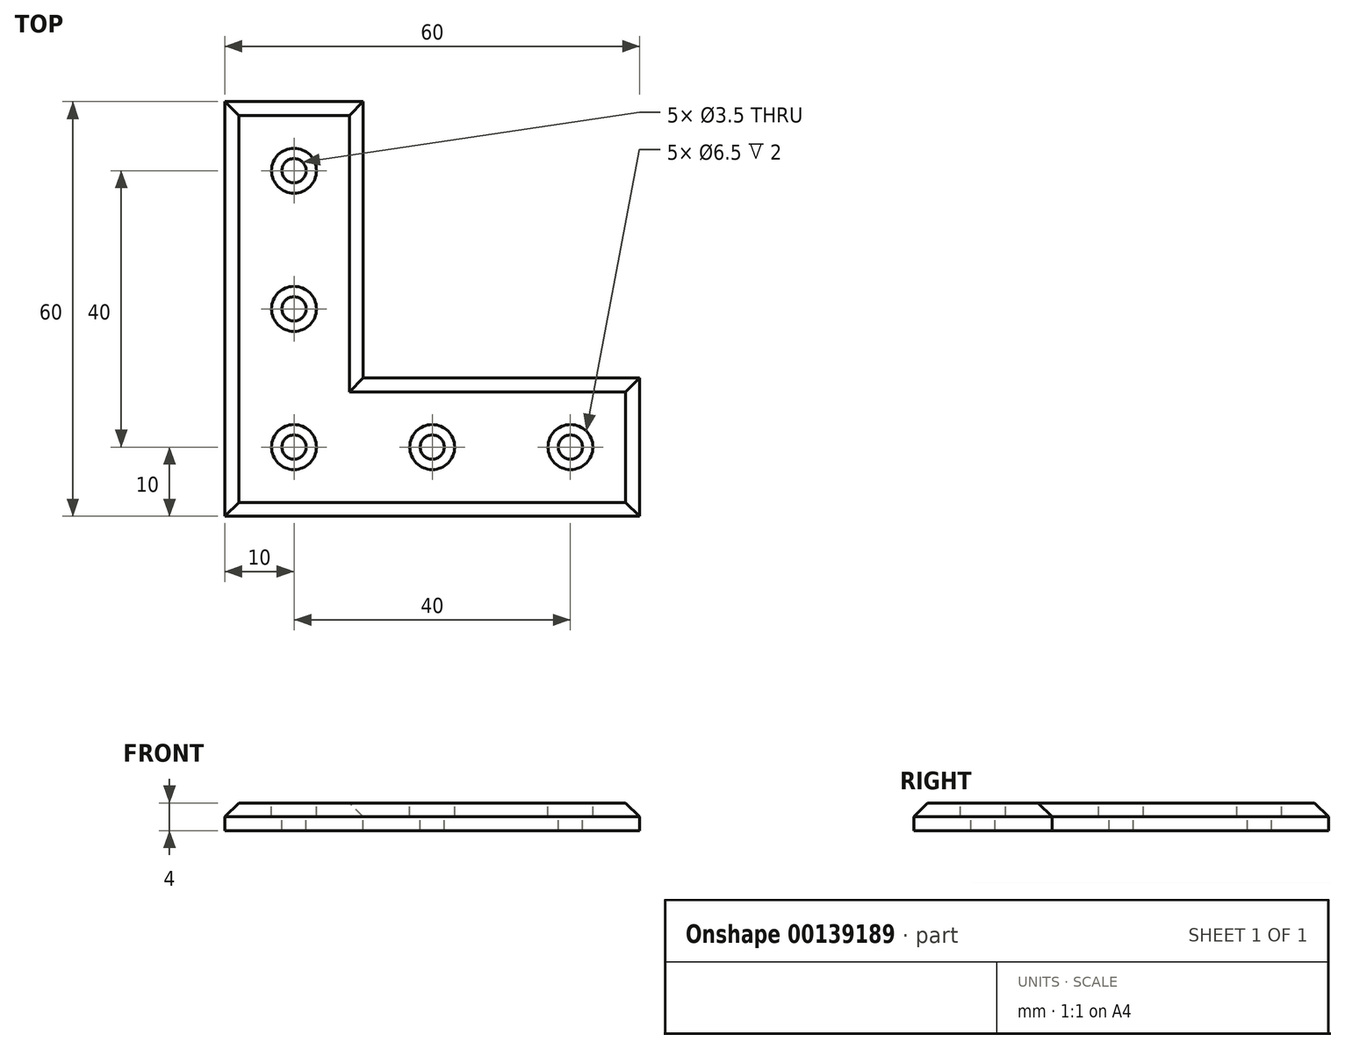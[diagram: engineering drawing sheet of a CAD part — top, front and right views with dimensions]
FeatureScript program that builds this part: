
annotation { "Feature Type Name" : "Feature", "Feature Type Description" : "" }
export const myFeature = defineFeature(function(context is Context, id is Id, definition is map)
    precondition{}
    {
        {
            assignVariable(context, id + "F0", {"name" : "Thickness", "anyValue" : 4});
        }
        {
            assignVariable(context, id + "F1", {"name" : "HeadHeight", "anyValue" : 2});
        }
        {
            var Q0;
            Q0=qCreatedBy(makeId("Top.planeOp"),FACE);
            var sketch = newSketch(context, id + "F2", { "sketchPlane" : qUnion([Q0])});
            skLineSegment(sketch, "E0", {"start": v(0, 0) * mm, "end": v(60, 0) * mm});
            skLineSegment(sketch, "E1", {"start": v(60, 0) * mm, "end": v(60, 20) * mm});
            skLineSegment(sketch, "E2", {"start": v(60, 20) * mm, "end": v(20, 20) * mm});
            skLineSegment(sketch, "E3", {"start": v(20, 20) * mm, "end": v(20, 60) * mm});
            skLineSegment(sketch, "E4", {"start": v(0, 0) * mm, "end": v(0, 60) * mm});
            skLineSegment(sketch, "E5", {"start": v(20, 60) * mm, "end": v(0, 60) * mm});
            skCircle(sketch, "E6", {"center": v(10, 10) * mm, "radius": 1.75 * mm});
            skPoint(sketch, "E6.centerSnap0", {"position": v(10, 60) * mm});
            skPoint(sketch, "E6.centerSnap1", {"position": v(60, 10) * mm});
            skCircle(sketch, "E7", {"center": v(10, 10) * mm, "radius": 3.25 * mm});
            skCircle(sketch, "E8", {"center": v(30, 10) * mm, "radius": 1.75 * mm});
            skCircle(sketch, "E9", {"center": v(30, 10) * mm, "radius": 3.25 * mm});
            skCircle(sketch, "E10", {"center": v(50, 10) * mm, "radius": 1.75 * mm});
            skCircle(sketch, "E11", {"center": v(50, 10) * mm, "radius": 3.25 * mm});
            skCircle(sketch, "E12", {"center": v(10, 30) * mm, "radius": 1.75 * mm});
            skCircle(sketch, "E13", {"center": v(10, 30) * mm, "radius": 3.25 * mm});
            skCircle(sketch, "E14", {"center": v(10, 50) * mm, "radius": 1.75 * mm});
            skCircle(sketch, "E15", {"center": v(10, 50) * mm, "radius": 3.25 * mm});
            skSolve(sketch);
        }
        {
            var Q0;
            Q0=makeQuery(id+"F2.imprint","IMPRINT",FACE,{"disambiguationData":[TD([[makeQuery(id+"F2.imprint","IMPRINT",EDGE,{"derivedFrom":sQuery(id+"F2.wireOp",EDGE,"E0")}),1.0]])]});
            var Q1;
            Q1=makeQuery(id+"F2.imprint","IMPRINT",FACE,{"disambiguationData":[TD([[makeQuery(id+"F2.imprint","IMPRINT",EDGE,{"derivedFrom":sQuery(id+"F2.wireOp",EDGE,"E14")}),-1.0]])]});
            var Q2;
            Q2=makeQuery(id+"F2.imprint","IMPRINT",FACE,{"disambiguationData":[TD([[makeQuery(id+"F2.imprint","IMPRINT",EDGE,{"derivedFrom":sQuery(id+"F2.wireOp",EDGE,"E14")}),1.0]])]});
            var Q3;
            Q3=makeQuery(id+"F2.imprint","IMPRINT",FACE,{"disambiguationData":[TD([[makeQuery(id+"F2.imprint","IMPRINT",EDGE,{"derivedFrom":sQuery(id+"F2.wireOp",EDGE,"E12")}),1.0]])]});
            var Q4;
            Q4=makeQuery(id+"F2.imprint","IMPRINT",FACE,{"disambiguationData":[TD([[makeQuery(id+"F2.imprint","IMPRINT",EDGE,{"derivedFrom":sQuery(id+"F2.wireOp",EDGE,"E12")}),-1.0]])]});
            var Q5;
            Q5=makeQuery(id+"F2.imprint","IMPRINT",FACE,{"disambiguationData":[TD([[makeQuery(id+"F2.imprint","IMPRINT",EDGE,{"derivedFrom":sQuery(id+"F2.wireOp",EDGE,"E6")}),-1.0]])]});
            var Q6;
            Q6=makeQuery(id+"F2.imprint","IMPRINT",FACE,{"disambiguationData":[TD([[makeQuery(id+"F2.imprint","IMPRINT",EDGE,{"derivedFrom":sQuery(id+"F2.wireOp",EDGE,"E6")}),1.0]])]});
            var Q7;
            Q7=makeQuery(id+"F2.imprint","IMPRINT",FACE,{"disambiguationData":[TD([[makeQuery(id+"F2.imprint","IMPRINT",EDGE,{"derivedFrom":sQuery(id+"F2.wireOp",EDGE,"E8")}),1.0]])]});
            var Q8;
            Q8=makeQuery(id+"F2.imprint","IMPRINT",FACE,{"disambiguationData":[TD([[makeQuery(id+"F2.imprint","IMPRINT",EDGE,{"derivedFrom":sQuery(id+"F2.wireOp",EDGE,"E8")}),-1.0]])]});
            var Q9;
            Q9=makeQuery(id+"F2.imprint","IMPRINT",FACE,{"disambiguationData":[TD([[makeQuery(id+"F2.imprint","IMPRINT",EDGE,{"derivedFrom":sQuery(id+"F2.wireOp",EDGE,"E10")}),-1.0]])]});
            var Q10;
            Q10=makeQuery(id+"F2.imprint","IMPRINT",FACE,{"disambiguationData":[TD([[makeQuery(id+"F2.imprint","IMPRINT",EDGE,{"derivedFrom":sQuery(id+"F2.wireOp",EDGE,"E10")}),1.0]])]});
            extrude(context, id + "F3", {"entities" : qUnion([Q0, Q1, Q2, Q3, Q4, Q5, Q6, Q7, Q8, Q9, Q10]), "oppositeDirection" : true, "depth" : (getVariable(context, 'Thickness')) * mm});
        }
        {
            var Q0;
            Q0=makeQuery(id+"F2.imprint","IMPRINT",FACE,{"disambiguationData":[TD([[makeQuery(id+"F2.imprint","IMPRINT",EDGE,{"derivedFrom":sQuery(id+"F2.wireOp",EDGE,"E14")}),1.0]])]});
            var Q1;
            Q1=makeQuery(id+"F2.imprint","IMPRINT",FACE,{"disambiguationData":[TD([[makeQuery(id+"F2.imprint","IMPRINT",EDGE,{"derivedFrom":sQuery(id+"F2.wireOp",EDGE,"E12")}),1.0]])]});
            var Q2;
            Q2=makeQuery(id+"F2.imprint","IMPRINT",FACE,{"disambiguationData":[TD([[makeQuery(id+"F2.imprint","IMPRINT",EDGE,{"derivedFrom":sQuery(id+"F2.wireOp",EDGE,"E6")}),1.0]])]});
            var Q3;
            Q3=makeQuery(id+"F2.imprint","IMPRINT",FACE,{"disambiguationData":[TD([[makeQuery(id+"F2.imprint","IMPRINT",EDGE,{"derivedFrom":sQuery(id+"F2.wireOp",EDGE,"E8")}),1.0]])]});
            var Q4;
            Q4=makeQuery(id+"F2.imprint","IMPRINT",FACE,{"disambiguationData":[TD([[makeQuery(id+"F2.imprint","IMPRINT",EDGE,{"derivedFrom":sQuery(id+"F2.wireOp",EDGE,"E10")}),1.0]])]});
            extrude(context, id + "F4", {"entities" : qUnion([Q0, Q1, Q2, Q3, Q4]), "operationType" : NewBodyOperationType.REMOVE, "endBound" : BoundingType.THROUGH_ALL, "oppositeDirection" : true, "depth" : 25 * mm});
        }
        {
            var Q0;
            Q0=makeQuery(id+"F2.imprint","IMPRINT",FACE,{"disambiguationData":[TD([[makeQuery(id+"F2.imprint","IMPRINT",EDGE,{"derivedFrom":sQuery(id+"F2.wireOp",EDGE,"E14")}),-1.0]])]});
            var Q1;
            Q1=makeQuery(id+"F2.imprint","IMPRINT",FACE,{"disambiguationData":[TD([[makeQuery(id+"F2.imprint","IMPRINT",EDGE,{"derivedFrom":sQuery(id+"F2.wireOp",EDGE,"E12")}),-1.0]])]});
            var Q2;
            Q2=makeQuery(id+"F2.imprint","IMPRINT",FACE,{"disambiguationData":[TD([[makeQuery(id+"F2.imprint","IMPRINT",EDGE,{"derivedFrom":sQuery(id+"F2.wireOp",EDGE,"E6")}),-1.0]])]});
            var Q3;
            Q3=makeQuery(id+"F2.imprint","IMPRINT",FACE,{"disambiguationData":[TD([[makeQuery(id+"F2.imprint","IMPRINT",EDGE,{"derivedFrom":sQuery(id+"F2.wireOp",EDGE,"E8")}),-1.0]])]});
            var Q4;
            Q4=makeQuery(id+"F2.imprint","IMPRINT",FACE,{"disambiguationData":[TD([[makeQuery(id+"F2.imprint","IMPRINT",EDGE,{"derivedFrom":sQuery(id+"F2.wireOp",EDGE,"E10")}),-1.0]])]});
            extrude(context, id + "F5", {"entities" : qUnion([Q0, Q1, Q2, Q3, Q4]), "operationType" : NewBodyOperationType.REMOVE, "oppositeDirection" : true, "depth" : (getVariable(context, 'HeadHeight')) * mm});
        }
        {
            var Q0;
            Q0=makeQuery(id+"F3.opExtrude","CAP_EDGE",EDGE,{"disambiguationData":[OSD([sQuery(id+"F2.wireOp",EDGE,"E2")])],"isStart":true});
            var Q1;
            Q1=makeQuery(id+"F3.opExtrude","CAP_EDGE",EDGE,{"disambiguationData":[OSD([sQuery(id+"F2.wireOp",EDGE,"E3")])],"isStart":true});
            var Q2;
            Q2=makeQuery(id+"F3.opExtrude","CAP_EDGE",EDGE,{"disambiguationData":[OSD([sQuery(id+"F2.wireOp",EDGE,"E5")])],"isStart":true});
            var Q3;
            Q3=makeQuery(id+"F3.opExtrude","CAP_EDGE",EDGE,{"disambiguationData":[OSD([sQuery(id+"F2.wireOp",EDGE,"E4")])],"isStart":true});
            var Q4;
            Q4=makeQuery(id+"F3.opExtrude","CAP_EDGE",EDGE,{"disambiguationData":[OSD([sQuery(id+"F2.wireOp",EDGE,"E0")])],"isStart":true});
            var Q5;
            Q5=makeQuery(id+"F3.opExtrude","CAP_EDGE",EDGE,{"disambiguationData":[OSD([sQuery(id+"F2.wireOp",EDGE,"E1")])],"isStart":true});
            chamfer(context, id + "F6", {"entities" : qUnion([Q0, Q1, Q2, Q3, Q4, Q5]), "width" : (getVariable(context, 'Thickness') / 2) * mm, "tangentPropagation" : true});
        }
    });
